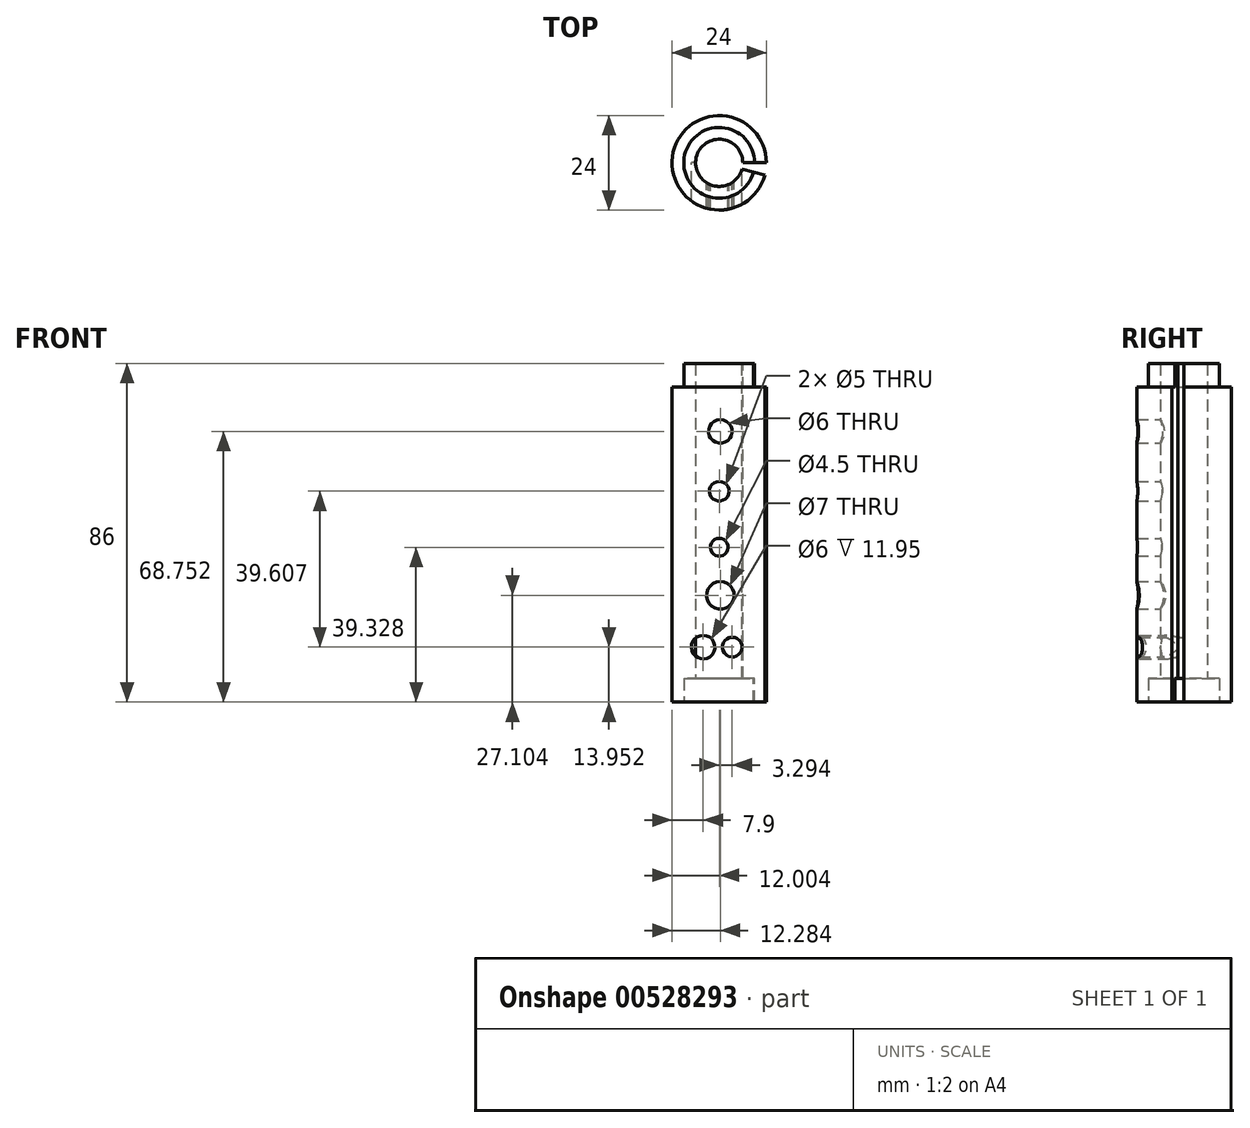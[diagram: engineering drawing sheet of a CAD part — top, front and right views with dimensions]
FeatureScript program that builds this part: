
annotation { "Feature Type Name" : "Feature", "Feature Type Description" : "" }
export const myFeature = defineFeature(function(context is Context, id is Id, definition is map)
    precondition{}
    {
        {
            var Q0;
            Q0=qCreatedBy(makeId("Front.planeOp"),FACE);
            var sketch = newSketch(context, id + "F0", { "sketchPlane" : qUnion([Q0])});
            skLineSegment(sketch, "E0", {"start": v(25.17, 20.88) * mm, "end": v(25.17, 100.88) * mm});
            skLineSegment(sketch, "E1", {"start": v(25.17, 100.88) * mm, "end": v(28.17, 100.88) * mm});
            skLineSegment(sketch, "E2", {"start": v(28.17, 100.88) * mm, "end": v(28.17, 94.88) * mm});
            skLineSegment(sketch, "E3", {"start": v(28.17, 94.88) * mm, "end": v(31.17, 94.88) * mm});
            skLineSegment(sketch, "E4", {"start": v(31.17, 94.88) * mm, "end": v(31.17, 14.88) * mm});
            skLineSegment(sketch, "E5", {"start": v(31.17, 14.88) * mm, "end": v(28.17, 14.88) * mm});
            skLineSegment(sketch, "E6", {"start": v(28.17, 14.88) * mm, "end": v(28.17, 20.88) * mm});
            skLineSegment(sketch, "E7", {"start": v(28.17, 20.88) * mm, "end": v(25.17, 20.88) * mm});
            skLineSegment(sketch, "E8", {"start": v(19.17, 75.4) * mm, "end": v(19.17, 0) * mm});
            skSolve(sketch);
        }
        {
            var Q0;
            Q0=makeQuery(id+"F0.imprint","IMPRINT",FACE,{"disambiguationData":[TD([[makeQuery(id+"F0.imprint","IMPRINT",EDGE,{"derivedFrom":sQuery(id+"F0.wireOp",EDGE,"E0")}),-1.0]])]});
            var Q1;
            Q1=sQuery(id+"F0.wireOp",EDGE,"E8");
            revolve(context, id + "F1", {"entities" : qUnion([Q0]), "axis" : qUnion([Q1]), "revolveType" : RevolveType.ONE_DIRECTION, "oppositeDirection" : true, "angle" : 345 * degree});
        }
        {
            var Q0;
            Q0=qCreatedBy(makeId("Front.planeOp"),FACE);
            var sketch = newSketch(context, id + "F2", { "sketchPlane" : qUnion([Q0])});
            skPoint(sketch, "E9", {"position": v(19.45, 83.63) * mm});
            skSolve(sketch);
        }
        {
            var Q0;
            Q0=qCreatedBy(makeId("Front.planeOp"),FACE);
            var sketch = newSketch(context, id + "F3", { "sketchPlane" : qUnion([Q0])});
            skPoint(sketch, "E10", {"position": v(19.17, 68.44) * mm});
            skSolve(sketch);
        }
        {
            var Q0;
            Q0=qCreatedBy(makeId("Front.planeOp"),FACE);
            var sketch = newSketch(context, id + "F4", { "sketchPlane" : qUnion([Q0])});
            skPoint(sketch, "E11", {"position": v(19.17, 54.2) * mm});
            skSolve(sketch);
        }
        {
            var Q0;
            Q0=qCreatedBy(makeId("Front.planeOp"),FACE);
            var sketch = newSketch(context, id + "F5", { "sketchPlane" : qUnion([Q0])});
            skPoint(sketch, "E12", {"position": v(19.45, 41.98) * mm});
            skSolve(sketch);
        }
        {
            var Q0;
            Q0=qCreatedBy(makeId("Front.planeOp"),FACE);
            var sketch = newSketch(context, id + "F6", { "sketchPlane" : qUnion([Q0])});
            skPoint(sketch, "E13", {"position": v(15.07, 28.83) * mm});
            skSolve(sketch);
        }
        {
            var Q0;
            Q0=qCreatedBy(makeId("Front.planeOp"),FACE);
            var sketch = newSketch(context, id + "F7", { "sketchPlane" : qUnion([Q0])});
            skPoint(sketch, "E14", {"position": v(22.47, 28.83) * mm});
            skSolve(sketch);
        }
        {
            var Q0;
            Q0=sQuery(id+"F2.wireOp",VERTEX,"E9");
            var Q1;
            Q1=makeQuery(id+"F1.opRevolve","SWEPT_BODY",BODY,{"disambiguationData":[OSD([sQuery(id+"F0.wireOp",EDGE,"E0"),sQuery(id+"F0.wireOp",EDGE,"E1"),sQuery(id+"F0.wireOp",EDGE,"E2"),sQuery(id+"F0.wireOp",EDGE,"E3"),sQuery(id+"F0.wireOp",EDGE,"E4"),sQuery(id+"F0.wireOp",EDGE,"E5"),sQuery(id+"F0.wireOp",EDGE,"E6"),sQuery(id+"F0.wireOp",EDGE,"E7")])]});
            hole(context, id + "F8", {"style" : HoleStyle.SIMPLE, "endStyle" : HoleEndStyle.THROUGH, "oppositeDirection" : true, "holeDiameter" : 6 * mm, "isTappedThrough" : true, "tappedDepth" : 12 * mm, "tapClearance" : 3, "locations" : qUnion([Q0]), "scope" : qUnion([Q1])});
        }
        {
            var Q0;
            Q0=sQuery(id+"F3.wireOp",VERTEX,"E10");
            var Q1;
            Q1=makeQuery(id+"F1.opRevolve","SWEPT_BODY",BODY,{"disambiguationData":[OSD([sQuery(id+"F0.wireOp",EDGE,"E0"),sQuery(id+"F0.wireOp",EDGE,"E1"),sQuery(id+"F0.wireOp",EDGE,"E2"),sQuery(id+"F0.wireOp",EDGE,"E3"),sQuery(id+"F0.wireOp",EDGE,"E4"),sQuery(id+"F0.wireOp",EDGE,"E5"),sQuery(id+"F0.wireOp",EDGE,"E6"),sQuery(id+"F0.wireOp",EDGE,"E7")])]});
            hole(context, id + "F9", {"style" : HoleStyle.SIMPLE, "endStyle" : HoleEndStyle.THROUGH, "oppositeDirection" : true, "holeDiameter" : 5 * mm, "isTappedThrough" : true, "tappedDepth" : 12 * mm, "tapClearance" : 3, "locations" : qUnion([Q0]), "scope" : qUnion([Q1])});
        }
        {
            var Q0;
            Q0=sQuery(id+"F4.wireOp",VERTEX,"E11");
            var Q1;
            Q1=makeQuery(id+"F1.opRevolve","SWEPT_BODY",BODY,{"disambiguationData":[OSD([sQuery(id+"F0.wireOp",EDGE,"E0"),sQuery(id+"F0.wireOp",EDGE,"E1"),sQuery(id+"F0.wireOp",EDGE,"E2"),sQuery(id+"F0.wireOp",EDGE,"E3"),sQuery(id+"F0.wireOp",EDGE,"E4"),sQuery(id+"F0.wireOp",EDGE,"E5"),sQuery(id+"F0.wireOp",EDGE,"E6"),sQuery(id+"F0.wireOp",EDGE,"E7")])]});
            hole(context, id + "F10", {"style" : HoleStyle.SIMPLE, "endStyle" : HoleEndStyle.THROUGH, "oppositeDirection" : true, "holeDiameter" : 4.5 * mm, "isTappedThrough" : true, "tappedDepth" : 12 * mm, "tapClearance" : 3, "locations" : qUnion([Q0]), "scope" : qUnion([Q1])});
        }
        {
            var Q0;
            Q0=sQuery(id+"F5.wireOp",VERTEX,"E12");
            var Q1;
            Q1=makeQuery(id+"F1.opRevolve","SWEPT_BODY",BODY,{"disambiguationData":[OSD([sQuery(id+"F0.wireOp",EDGE,"E0"),sQuery(id+"F0.wireOp",EDGE,"E1"),sQuery(id+"F0.wireOp",EDGE,"E2"),sQuery(id+"F0.wireOp",EDGE,"E3"),sQuery(id+"F0.wireOp",EDGE,"E4"),sQuery(id+"F0.wireOp",EDGE,"E5"),sQuery(id+"F0.wireOp",EDGE,"E6"),sQuery(id+"F0.wireOp",EDGE,"E7")])]});
            hole(context, id + "F11", {"style" : HoleStyle.SIMPLE, "endStyle" : HoleEndStyle.THROUGH, "oppositeDirection" : true, "holeDiameter" : 7 * mm, "isTappedThrough" : true, "tappedDepth" : 12 * mm, "tapClearance" : 3, "locations" : qUnion([Q0]), "scope" : qUnion([Q1])});
        }
        {
            var Q0;
            Q0=sQuery(id+"F6.wireOp",VERTEX,"E13");
            var Q1;
            Q1=makeQuery(id+"F1.opRevolve","SWEPT_BODY",BODY,{"disambiguationData":[OSD([sQuery(id+"F0.wireOp",EDGE,"E0"),sQuery(id+"F0.wireOp",EDGE,"E1"),sQuery(id+"F0.wireOp",EDGE,"E2"),sQuery(id+"F0.wireOp",EDGE,"E3"),sQuery(id+"F0.wireOp",EDGE,"E4"),sQuery(id+"F0.wireOp",EDGE,"E5"),sQuery(id+"F0.wireOp",EDGE,"E6"),sQuery(id+"F0.wireOp",EDGE,"E7")])]});
            hole(context, id + "F12", {"style" : HoleStyle.SIMPLE, "endStyle" : HoleEndStyle.THROUGH, "oppositeDirection" : true, "holeDiameter" : 6 * mm, "isTappedThrough" : true, "tappedDepth" : 12 * mm, "tapClearance" : 3, "locations" : qUnion([Q0]), "scope" : qUnion([Q1])});
        }
        {
            var Q0;
            Q0=sQuery(id+"F7.wireOp",VERTEX,"E14");
            var Q1;
            Q1=makeQuery(id+"F1.opRevolve","SWEPT_BODY",BODY,{"disambiguationData":[OSD([sQuery(id+"F0.wireOp",EDGE,"E0"),sQuery(id+"F0.wireOp",EDGE,"E1"),sQuery(id+"F0.wireOp",EDGE,"E2"),sQuery(id+"F0.wireOp",EDGE,"E3"),sQuery(id+"F0.wireOp",EDGE,"E4"),sQuery(id+"F0.wireOp",EDGE,"E5"),sQuery(id+"F0.wireOp",EDGE,"E6"),sQuery(id+"F0.wireOp",EDGE,"E7")])]});
            hole(context, id + "F13", {"style" : HoleStyle.SIMPLE, "endStyle" : HoleEndStyle.THROUGH, "oppositeDirection" : true, "holeDiameter" : 5 * mm, "isTappedThrough" : true, "tappedDepth" : 12 * mm, "tapClearance" : 3, "locations" : qUnion([Q0]), "scope" : qUnion([Q1])});
        }
    });
